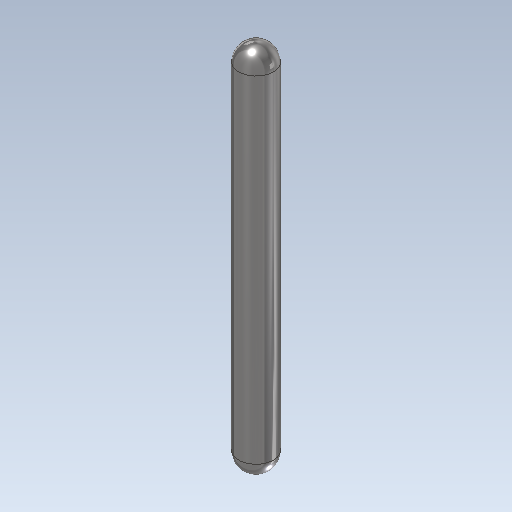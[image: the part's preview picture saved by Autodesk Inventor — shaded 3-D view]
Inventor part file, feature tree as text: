
AUTODESK INVENTOR PART (.ipt)
format: ipt  version: 2020 (Build 240168000, 168)  size: 99,840 bytes
history: native  units: in
note: dims shown in document units (in); Inventor stores cm internally (conversion verified against a paired STEP export)
features: extrude x1, fillet x1, sketch x1
ambient origin geometry x7: Origin, YZ Plane, XZ Plane, X Axis, Y Axis, Z Axis, Center Point
bodies: Solid1 (feature_tree)
feature tree (3):
  extrude  "Midplane_HP"  Depth=0.0115in
  fillet  "Fillet2"  Radius=0.0115in
  sketch  "Sketch1-<F>"  dims[d0=0.245in d1=0.0in d3=0.023in d4=0.0115in]
